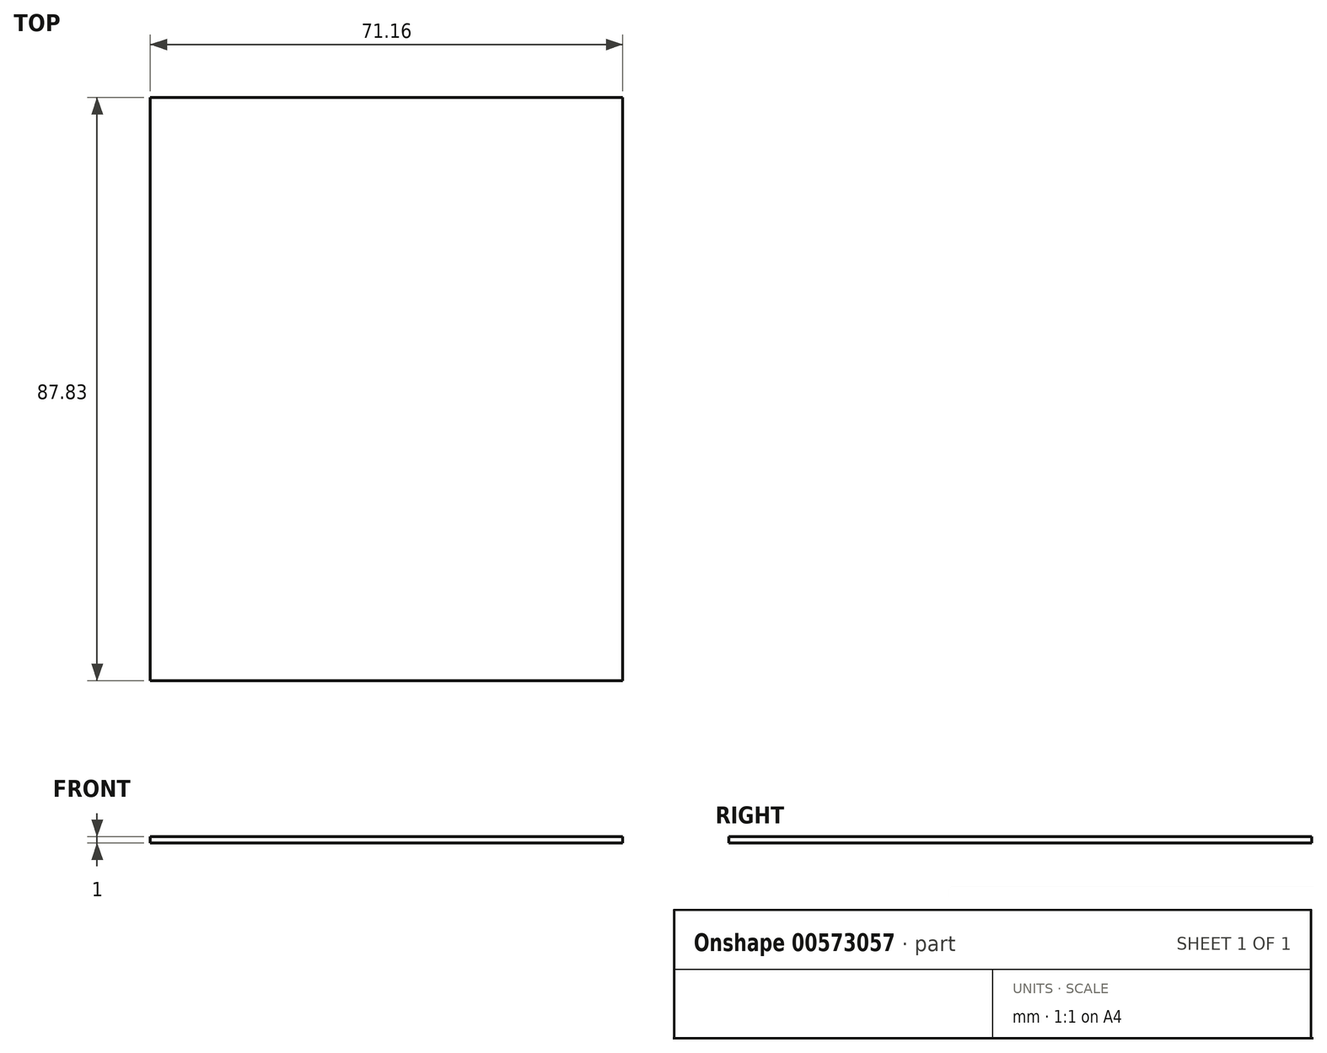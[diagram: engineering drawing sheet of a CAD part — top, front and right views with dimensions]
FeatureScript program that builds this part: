
annotation { "Feature Type Name" : "Feature", "Feature Type Description" : "" }
export const myFeature = defineFeature(function(context is Context, id is Id, definition is map)
    precondition{}
    {
        {
            var Q0;
            Q0=qCreatedBy(makeId("Top.planeOp"),FACE);
            var sketch = newSketch(context, id + "F0", { "sketchPlane" : qUnion([Q0])});
            skLineSegment(sketch, "E0.bottom", {"start": v(-60.77, 60.4) * mm, "end": v(10.39, 60.4) * mm});
            skLineSegment(sketch, "E0.top", {"start": v(-60.77, -27.43) * mm, "end": v(10.39, -27.43) * mm});
            skLineSegment(sketch, "E0.left", {"start": v(-60.77, 60.4) * mm, "end": v(-60.77, -27.43) * mm});
            skLineSegment(sketch, "E0.right", {"start": v(10.39, 60.4) * mm, "end": v(10.39, -27.43) * mm});
            skSolve(sketch);
        }
        {
            var Q0;
            Q0=makeQuery(id+"F0.imprint","IMPRINT",FACE,{"disambiguationData":[TD([[makeQuery(id+"F0.imprint","IMPRINT",EDGE,{"derivedFrom":sQuery(id+"F0.wireOp",EDGE,"E0.bottom")}),-1.0]])]});
            extrude(context, id + "F1", {"entities" : qUnion([Q0]), "depth" : 1 * mm, "offsetDistance" : 25 * mm});
        }
    });
